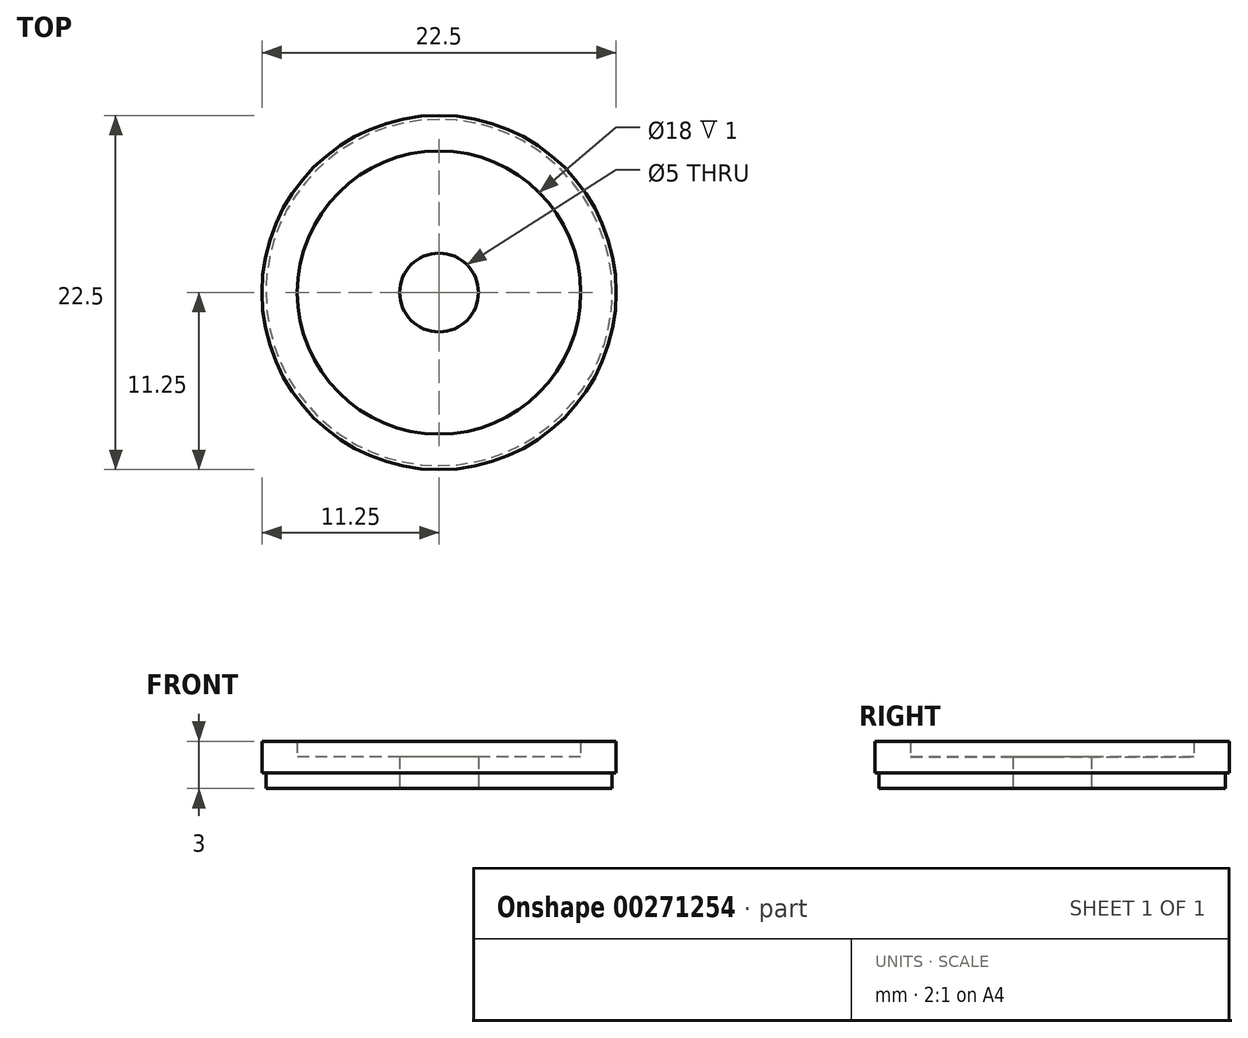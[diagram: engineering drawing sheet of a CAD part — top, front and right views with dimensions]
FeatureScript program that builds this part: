
annotation { "Feature Type Name" : "Feature", "Feature Type Description" : "" }
export const myFeature = defineFeature(function(context is Context, id is Id, definition is map)
    precondition{}
    {
        {
            var Q0;
            Q0=qCreatedBy(makeId("Top.planeOp"),FACE);
            var sketch = newSketch(context, id + "F0", { "sketchPlane" : qUnion([Q0])});
            skCircle(sketch, "E0", {"center": v(0, 0) * mm, "radius": 11.25 * mm});
            skCircle(sketch, "E1", {"center": v(0, 0) * mm, "radius": 9 * mm});
            skCircle(sketch, "E2", {"center": v(0, 0) * mm, "radius": 2.5 * mm});
            skLineSegment(sketch, "E3", {"start": v(0, 0) * mm, "end": v(0, 9) * mm});
            skLineSegment(sketch, "E4", {"start": v(0, 9) * mm, "end": v(0, 0) * mm});
            skLineSegment(sketch, "E5", {"start": v(0, 0) * mm, "end": v(9, 0) * mm});
            skLineSegment(sketch, "E6", {"start": v(9, 0) * mm, "end": v(0, 0) * mm});
            skLineSegment(sketch, "E7", {"start": v(0, 0) * mm, "end": v(0, -9) * mm});
            skLineSegment(sketch, "E8", {"start": v(0, -9) * mm, "end": v(0, 0) * mm});
            skLineSegment(sketch, "E9", {"start": v(0, 0) * mm, "end": v(-9, 0) * mm});
            skLineSegment(sketch, "E10", {"start": v(-9, 0) * mm, "end": v(0, 0) * mm});
            skLineSegment(sketch, "E11", {"start": v(0, 0) * mm, "end": v(4.5, 7.8) * mm});
            skLineSegment(sketch, "E12", {"start": v(4.5, 7.8) * mm, "end": v(0, 0) * mm});
            skLineSegment(sketch, "E13", {"start": v(0, 0) * mm, "end": v(7.8, 4.5) * mm});
            skLineSegment(sketch, "E14", {"start": v(7.8, 4.5) * mm, "end": v(0, 0) * mm});
            skLineSegment(sketch, "E15", {"start": v(0, 0) * mm, "end": v(7.8, -4.5) * mm});
            skLineSegment(sketch, "E16", {"start": v(7.8, -4.5) * mm, "end": v(0, 0) * mm});
            skLineSegment(sketch, "E17", {"start": v(0, 0) * mm, "end": v(4.5, -7.8) * mm});
            skLineSegment(sketch, "E18", {"start": v(4.5, -7.8) * mm, "end": v(0, 0) * mm});
            skLineSegment(sketch, "E19", {"start": v(0, 0) * mm, "end": v(-4.5, -7.8) * mm});
            skLineSegment(sketch, "E20", {"start": v(-4.5, -7.8) * mm, "end": v(0, 0) * mm});
            skLineSegment(sketch, "E21", {"start": v(0, 0) * mm, "end": v(-7.8, -4.5) * mm});
            skLineSegment(sketch, "E22", {"start": v(-7.8, -4.5) * mm, "end": v(0, 0) * mm});
            skLineSegment(sketch, "E23", {"start": v(0, 0) * mm, "end": v(-7.8, 4.5) * mm});
            skLineSegment(sketch, "E24", {"start": v(-7.8, 4.5) * mm, "end": v(0, 0) * mm});
            skLineSegment(sketch, "E25", {"start": v(0, 0) * mm, "end": v(-4.5, 7.8) * mm});
            skLineSegment(sketch, "E26", {"start": v(-4.5, 7.8) * mm, "end": v(0, 0) * mm});
            skSolve(sketch);
        }
        {
            var Q0;
            Q0=makeQuery(id+"F0.imprint","IMPRINT",FACE,{"disambiguationData":[TD([[makeQuery(id+"F0.imprint","IMPRINT",EDGE,{"derivedFrom":sQuery(id+"F0.wireOp",EDGE,"E0")}),1.0]])]});
            extrude(context, id + "F1", {"entities" : qUnion([Q0]), "depth" : 3 * mm});
        }
        {
            var Q0;
            {var subQ0=sQuery(id+"F0.wireOp",EDGE,"E24");var subQ1=sQuery(id+"F0.wireOp",EDGE,"E1");var subQ2=makeQuery(id+"F0.imprint","INTERSECT",VERTEX,{"derivedFrom":[subQ1,subQ0]});Q0=makeQuery(id+"F0.imprint","IMPRINT",FACE,{"disambiguationData":[TD([[makeQuery(id+"F0.imprint","IMPRINT",EDGE,{"disambiguationData":[TD([[subQ2,1.0]])],"derivedFrom":subQ1}),1.0]])]});}
            var Q1;
            {var subQ0=sQuery(id+"F0.wireOp",EDGE,"E4");var subQ1=sQuery(id+"F0.wireOp",EDGE,"E1");var subQ2=makeQuery(id+"F0.imprint","INTERSECT",VERTEX,{"derivedFrom":[subQ1,subQ0]});Q1=makeQuery(id+"F0.imprint","IMPRINT",FACE,{"disambiguationData":[TD([[makeQuery(id+"F0.imprint","IMPRINT",EDGE,{"disambiguationData":[TD([[subQ2,1.0]])],"derivedFrom":subQ1}),1.0]])]});}
            var Q2;
            {var subQ0=sQuery(id+"F0.wireOp",EDGE,"E6");var subQ1=sQuery(id+"F0.wireOp",EDGE,"E1");var subQ2=makeQuery(id+"F0.imprint","INTERSECT",VERTEX,{"derivedFrom":[subQ1,subQ0]});Q2=makeQuery(id+"F0.imprint","IMPRINT",FACE,{"disambiguationData":[TD([[makeQuery(id+"F0.imprint","IMPRINT",EDGE,{"disambiguationData":[TD([[subQ2,-1.0]])],"derivedFrom":subQ1}),1.0]])]});}
            var Q3;
            {var subQ0=sQuery(id+"F0.wireOp",EDGE,"E16");var subQ1=sQuery(id+"F0.wireOp",EDGE,"E1");var subQ2=makeQuery(id+"F0.imprint","INTERSECT",VERTEX,{"derivedFrom":[subQ1,subQ0]});Q3=makeQuery(id+"F0.imprint","IMPRINT",FACE,{"disambiguationData":[TD([[makeQuery(id+"F0.imprint","IMPRINT",EDGE,{"disambiguationData":[TD([[subQ2,1.0]])],"derivedFrom":subQ1}),1.0]])]});}
            var Q4;
            {var subQ0=sQuery(id+"F0.wireOp",EDGE,"E8");var subQ1=sQuery(id+"F0.wireOp",EDGE,"E1");var subQ2=makeQuery(id+"F0.imprint","INTERSECT",VERTEX,{"derivedFrom":[subQ1,subQ0]});Q4=makeQuery(id+"F0.imprint","IMPRINT",FACE,{"disambiguationData":[TD([[makeQuery(id+"F0.imprint","IMPRINT",EDGE,{"disambiguationData":[TD([[subQ2,1.0]])],"derivedFrom":subQ1}),1.0]])]});}
            var Q5;
            {var subQ0=sQuery(id+"F0.wireOp",EDGE,"E10");var subQ1=sQuery(id+"F0.wireOp",EDGE,"E1");var subQ2=makeQuery(id+"F0.imprint","INTERSECT",VERTEX,{"derivedFrom":[subQ1,subQ0]});Q5=makeQuery(id+"F0.imprint","IMPRINT",FACE,{"disambiguationData":[TD([[makeQuery(id+"F0.imprint","IMPRINT",EDGE,{"disambiguationData":[TD([[subQ2,-1.0]])],"derivedFrom":subQ1}),1.0]])]});}
            extrude(context, id + "F2", {"entities" : qUnion([Q0, Q1, Q2, Q3, Q4, Q5]), "operationType" : NewBodyOperationType.ADD, "depth" : 2 * mm});
        }
        {
            var Q0;
            {var subQ0=sQuery(id+"F0.wireOp",EDGE,"E10");var subQ1=sQuery(id+"F0.wireOp",EDGE,"E1");var subQ2=makeQuery(id+"F0.imprint","INTERSECT",VERTEX,{"derivedFrom":[subQ1,subQ0]});Q0=makeQuery(id+"F0.imprint","IMPRINT",FACE,{"disambiguationData":[TD([[makeQuery(id+"F0.imprint","IMPRINT",EDGE,{"disambiguationData":[TD([[subQ2,1.0]])],"derivedFrom":subQ1}),1.0]])]});}
            var Q1;
            {var subQ0=sQuery(id+"F0.wireOp",EDGE,"E4");var subQ1=sQuery(id+"F0.wireOp",EDGE,"E1");var subQ2=makeQuery(id+"F0.imprint","INTERSECT",VERTEX,{"derivedFrom":[subQ1,subQ0]});Q1=makeQuery(id+"F0.imprint","IMPRINT",FACE,{"disambiguationData":[TD([[makeQuery(id+"F0.imprint","IMPRINT",EDGE,{"disambiguationData":[TD([[subQ2,-1.0]])],"derivedFrom":subQ1}),1.0]])]});}
            var Q2;
            {var subQ0=sQuery(id+"F0.wireOp",EDGE,"E12");var subQ1=sQuery(id+"F0.wireOp",EDGE,"E1");var subQ2=makeQuery(id+"F0.imprint","INTERSECT",VERTEX,{"derivedFrom":[subQ1,subQ0]});Q2=makeQuery(id+"F0.imprint","IMPRINT",FACE,{"disambiguationData":[TD([[makeQuery(id+"F0.imprint","IMPRINT",EDGE,{"disambiguationData":[TD([[subQ2,1.0]])],"derivedFrom":subQ1}),1.0]])]});}
            var Q3;
            {var subQ0=sQuery(id+"F0.wireOp",EDGE,"E6");var subQ1=sQuery(id+"F0.wireOp",EDGE,"E1");var subQ2=makeQuery(id+"F0.imprint","INTERSECT",VERTEX,{"derivedFrom":[subQ1,subQ0]});Q3=makeQuery(id+"F0.imprint","IMPRINT",FACE,{"disambiguationData":[TD([[makeQuery(id+"F0.imprint","IMPRINT",EDGE,{"disambiguationData":[TD([[subQ2,1.0]])],"derivedFrom":subQ1}),1.0]])]});}
            var Q4;
            {var subQ0=sQuery(id+"F0.wireOp",EDGE,"E8");var subQ1=sQuery(id+"F0.wireOp",EDGE,"E1");var subQ2=makeQuery(id+"F0.imprint","INTERSECT",VERTEX,{"derivedFrom":[subQ1,subQ0]});Q4=makeQuery(id+"F0.imprint","IMPRINT",FACE,{"disambiguationData":[TD([[makeQuery(id+"F0.imprint","IMPRINT",EDGE,{"disambiguationData":[TD([[subQ2,-1.0]])],"derivedFrom":subQ1}),1.0]])]});}
            var Q5;
            {var subQ0=sQuery(id+"F0.wireOp",EDGE,"E20");var subQ1=sQuery(id+"F0.wireOp",EDGE,"E1");var subQ2=makeQuery(id+"F0.imprint","INTERSECT",VERTEX,{"derivedFrom":[subQ1,subQ0]});Q5=makeQuery(id+"F0.imprint","IMPRINT",FACE,{"disambiguationData":[TD([[makeQuery(id+"F0.imprint","IMPRINT",EDGE,{"disambiguationData":[TD([[subQ2,1.0]])],"derivedFrom":subQ1}),1.0]])]});}
            extrude(context, id + "F3", {"entities" : qUnion([Q0, Q1, Q2, Q3, Q4, Q5]), "operationType" : NewBodyOperationType.ADD, "depth" : 1.5 * mm});
        }
        {
            var Q0;
            {var subQ0=sQuery(id+"F0.wireOp",EDGE,"E16");var subQ1=sQuery(id+"F0.wireOp",EDGE,"E6");var subQ2=sQuery(id+"F0.wireOp",EDGE,"E2");var subQ3=sQuery(id+"F0.wireOp",EDGE,"E1");var subQ4=sQuery(id+"F0.wireOp",EDGE,"E18");var subQ5=sQuery(id+"F0.wireOp",EDGE,"E8");var subQ6=sQuery(id+"F0.wireOp",EDGE,"E22");var subQ7=sQuery(id+"F0.wireOp",EDGE,"E20");var subQ8=sQuery(id+"F0.wireOp",EDGE,"E24");var subQ9=sQuery(id+"F0.wireOp",EDGE,"E10");var subQ10=sQuery(id+"F0.wireOp",EDGE,"E26");var subQ11=sQuery(id+"F0.wireOp",EDGE,"E4");var subQ12=sQuery(id+"F0.wireOp",EDGE,"E14");var subQ13=sQuery(id+"F0.wireOp",EDGE,"E12");Q0=makeQuery(id+"F3.boolean.opBoolean","MERGE",FACE,{"derivedFrom":[makeQuery(id+"F2.boolean.opBoolean","MERGE",FACE,{"derivedFrom":[makeQuery(id+"F1.opExtrude","CAP_FACE",FACE,{"disambiguationData":[OSD([sQuery(id+"F0.wireOp",EDGE,"E0"),subQ3])],"isStart":true}),makeQuery(id+"F2.opExtrude","CAP_FACE",FACE,{"disambiguationData":[OSD([subQ3,subQ2,subQ1,subQ12])],"isStart":true}),makeQuery(id+"F2.opExtrude","CAP_FACE",FACE,{"disambiguationData":[OSD([subQ3,subQ2,subQ11,subQ13])],"isStart":true}),makeQuery(id+"F2.opExtrude","CAP_FACE",FACE,{"disambiguationData":[OSD([subQ3,subQ2,subQ8,subQ10])],"isStart":true}),makeQuery(id+"F2.opExtrude","CAP_FACE",FACE,{"disambiguationData":[OSD([subQ3,subQ2,subQ9,subQ6])],"isStart":true}),makeQuery(id+"F2.opExtrude","CAP_FACE",FACE,{"disambiguationData":[OSD([subQ3,subQ2,subQ5,subQ7])],"isStart":true}),makeQuery(id+"F2.opExtrude","CAP_FACE",FACE,{"disambiguationData":[OSD([subQ3,subQ2,subQ0,subQ4])],"isStart":true})]}),makeQuery(id+"F3.opExtrude","CAP_FACE",FACE,{"disambiguationData":[OSD([subQ3,subQ2,subQ13,subQ12])],"isStart":true}),makeQuery(id+"F3.opExtrude","CAP_FACE",FACE,{"disambiguationData":[OSD([subQ3,subQ2,subQ11,subQ10])],"isStart":true}),makeQuery(id+"F3.opExtrude","CAP_FACE",FACE,{"disambiguationData":[OSD([subQ3,subQ2,subQ9,subQ8])],"isStart":true}),makeQuery(id+"F3.opExtrude","CAP_FACE",FACE,{"disambiguationData":[OSD([subQ3,subQ2,subQ7,subQ6])],"isStart":true}),makeQuery(id+"F3.opExtrude","CAP_FACE",FACE,{"disambiguationData":[OSD([subQ3,subQ2,subQ5,subQ4])],"isStart":true}),makeQuery(id+"F3.opExtrude","CAP_FACE",FACE,{"disambiguationData":[OSD([subQ3,subQ2,subQ1,subQ0])],"isStart":true})]});}
            var sketch = newSketch(context, id + "F4", { "sketchPlane" : qUnion([Q0])});
            skCircle(sketch, "E27", {"center": v(0, 0) * mm, "radius": 11.25 * mm});
            skCircle(sketch, "E28", {"center": v(0, 0) * mm, "radius": 11 * mm});
            skSolve(sketch);
        }
        {
            var Q0;
            Q0=makeQuery(id+"F4.imprint","IMPRINT",FACE,{"disambiguationData":[TD([[makeQuery(id+"F4.imprint","IMPRINT",EDGE,{"derivedFrom":sQuery(id+"F4.wireOp",EDGE,"E27")}),-1.0]])]});
            extrude(context, id + "F5", {"entities" : qUnion([Q0]), "operationType" : NewBodyOperationType.REMOVE, "oppositeDirection" : true, "depth" : 1 * mm});
        }
    });
